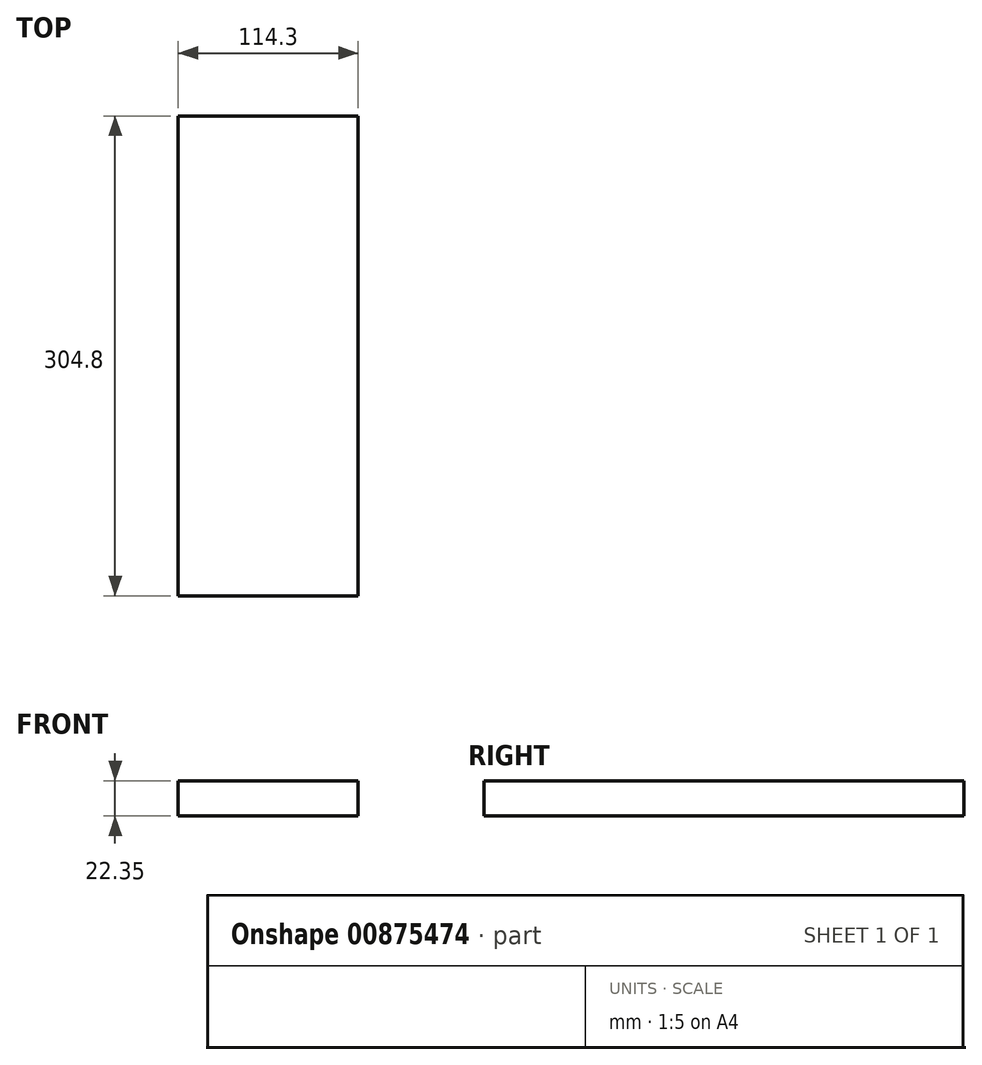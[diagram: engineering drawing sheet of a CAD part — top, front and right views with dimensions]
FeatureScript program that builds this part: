
annotation { "Feature Type Name" : "Feature", "Feature Type Description" : "" }
export const myFeature = defineFeature(function(context is Context, id is Id, definition is map)
    precondition{}
    {
        {
            var Q0;
            Q0=qCreatedBy(makeId("Front.planeOp"),FACE);
            var sketch = newSketch(context, id + "F0", { "sketchPlane" : qUnion([Q0])});
            skLineSegment(sketch, "E0.bottom", {"start": v(-76.92, -62.06) * mm, "end": v(37.38, -62.06) * mm});
            skLineSegment(sketch, "E0.top", {"start": v(-76.92, -84.4) * mm, "end": v(37.38, -84.4) * mm});
            skLineSegment(sketch, "E0.left", {"start": v(-76.92, -62.06) * mm, "end": v(-76.92, -84.4) * mm});
            skLineSegment(sketch, "E0.right", {"start": v(37.38, -62.06) * mm, "end": v(37.38, -84.4) * mm});
            skSolve(sketch);
        }
        {
            var Q0;
            Q0=makeQuery(id+"F0.imprint","IMPRINT",FACE,{"disambiguationData":[TD([[makeQuery(id+"F0.imprint","IMPRINT",EDGE,{"derivedFrom":sQuery(id+"F0.wireOp",EDGE,"E0.bottom")}),-1.0]])]});
            extrude(context, id + "F1", {"entities" : qUnion([Q0]), "depth" : 304.8 * mm, "offsetDistance" : 25.4 * mm});
        }
    });
